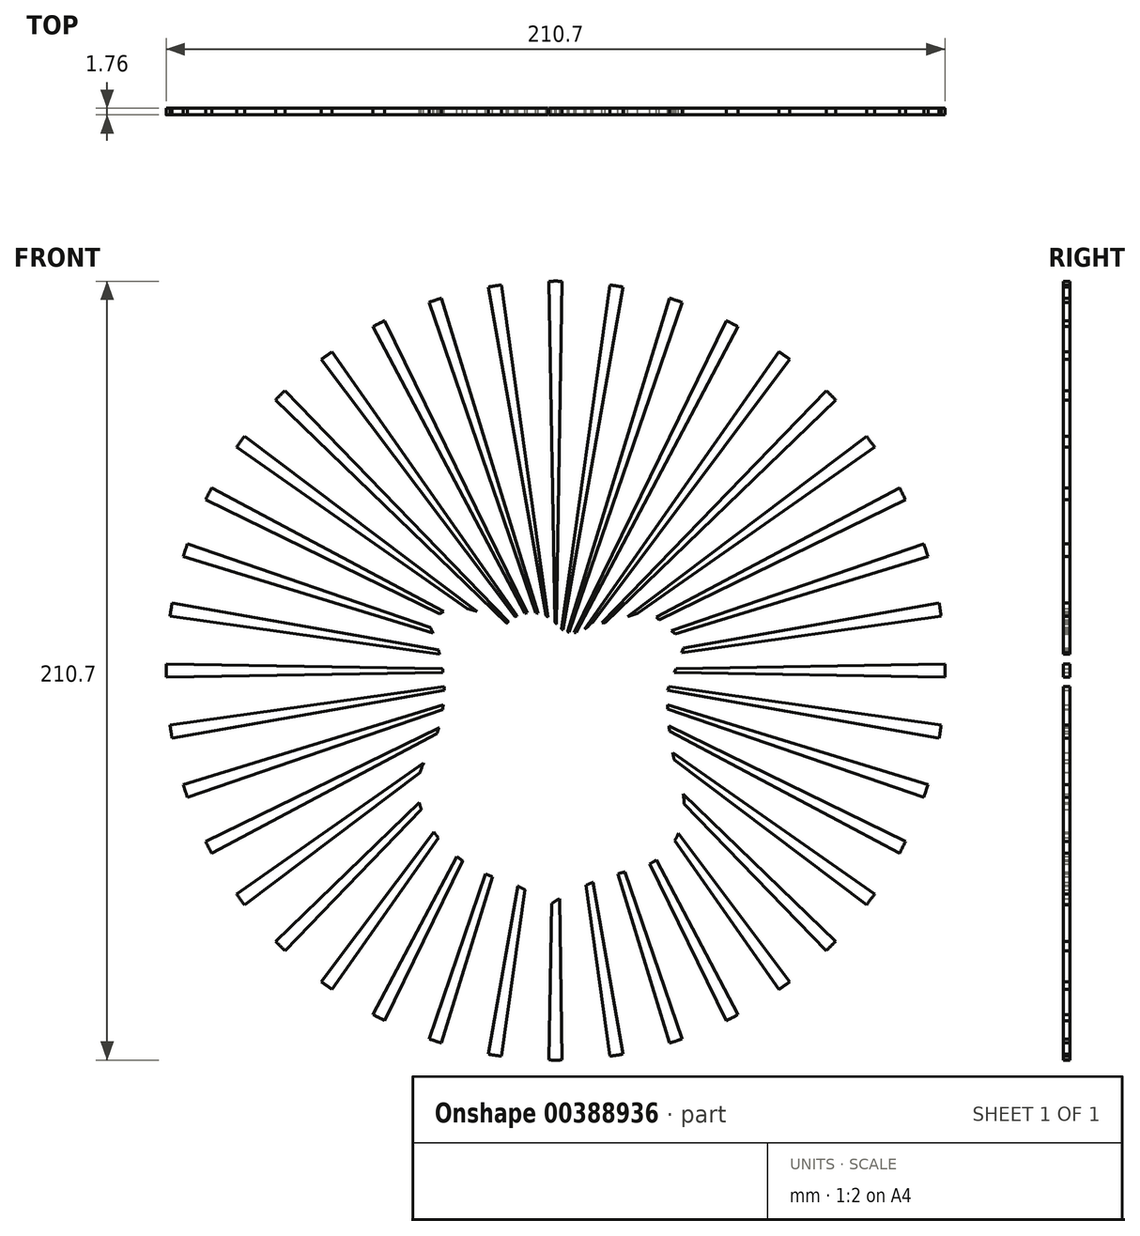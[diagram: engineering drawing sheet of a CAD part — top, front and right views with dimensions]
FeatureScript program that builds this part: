
annotation { "Feature Type Name" : "Feature", "Feature Type Description" : "" }
export const myFeature = defineFeature(function(context is Context, id is Id, definition is map)
    precondition{}
    {
        {
            var Q0;
            Q0=qCreatedBy(makeId("Front.planeOp"),FACE);
            var sketch = newSketch(context, id + "F0", { "sketchPlane" : qUnion([Q0])});
            skCircle(sketch, "E0", {"center": v(1.46, 6.02) * mm, "radius": 39.02 * mm});
            skArc(sketch, "E1", {"start": v(0.74, -17.53) * mm, "mid": v(0.64, -17.44) * mm, "end": v(0.54, -17.36) * mm});
            skArc(sketch, "E2", {"start": v(9.18, -13.96) * mm, "mid": v(8.33, -14.17) * mm, "end": v(7.5, -14.4) * mm});
            skArc(sketch, "E3", {"start": v(9.18, -13.96) * mm, "mid": v(9.38, -13.92) * mm, "end": v(9.59, -13.87) * mm});
            skArc(sketch, "E4", {"start": v(12.7, 4.03) * mm, "mid": v(12.69, 3.1) * mm, "end": v(12.71, 2.18) * mm});
            skArc(sketch, "E5", {"start": v(-10.42, 8.53) * mm, "mid": v(-10.48, 8.8) * mm, "end": v(-10.55, 9.05) * mm});
            skLineSegment(sketch, "E6", {"start": v(-8.79, 12.6) * mm, "end": v(-7.7, 12.3) * mm});
            skLineSegment(sketch, "E7", {"start": v(-4.49, 11.42) * mm, "end": v(-4.05, 10.9) * mm});
            skArc(sketch, "E8", {"start": v(1.46, 10.8) * mm, "mid": v(1.12, 11.12) * mm, "end": v(0.73, 11.38) * mm});
            skArc(sketch, "E9", {"start": v(1.46, 10.8) * mm, "mid": v(1.68, 10.53) * mm, "end": v(1.93, 10.29) * mm});
            skLineSegment(sketch, "E10", {"start": v(5, 10.8) * mm, "end": v(5.12, 10.8) * mm});
            skArc(sketch, "E11", {"start": v(-3.04, -15.26) * mm, "mid": v(-3.45, -15.1) * mm, "end": v(-3.87, -14.95) * mm});
            skArc(sketch, "E12", {"start": v(-1.52, -15.98) * mm, "mid": v(-2.27, -15.6) * mm, "end": v(-3.04, -15.26) * mm});
            skArc(sketch, "E13", {"start": v(-0.45, -16.63) * mm, "mid": v(-0.98, -16.3) * mm, "end": v(-1.52, -15.98) * mm});
            skArc(sketch, "E14", {"start": v(0.54, -17.36) * mm, "mid": v(0.05, -16.98) * mm, "end": v(-0.45, -16.63) * mm});
            skArc(sketch, "E15", {"start": v(3.46, -15.97) * mm, "mid": v(2.08, -16.7) * mm, "end": v(0.74, -17.53) * mm});
            skArc(sketch, "E16", {"start": v(5.93, -14.91) * mm, "mid": v(4.68, -15.4) * mm, "end": v(3.46, -15.97) * mm});
            skArc(sketch, "E17", {"start": v(9.59, -13.87) * mm, "mid": v(13.32, -11.14) * mm, "end": v(14.29, -6.62) * mm});
            skArc(sketch, "E18", {"start": v(13.65, -4.21) * mm, "mid": v(13.84, -4.9) * mm, "end": v(14.04, -5.6) * mm});
            skArc(sketch, "E19", {"start": v(12.96, -0.68) * mm, "mid": v(13.11, -1.71) * mm, "end": v(13.3, -2.74) * mm});
            skArc(sketch, "E20", {"start": v(12.83, 0.44) * mm, "mid": v(12.89, -0.12) * mm, "end": v(12.96, -0.68) * mm});
            skArc(sketch, "E21", {"start": v(12.71, 2.18) * mm, "mid": v(12.76, 1.3) * mm, "end": v(12.83, 0.44) * mm});
            skArc(sketch, "E22", {"start": v(13.3, -2.74) * mm, "mid": v(13.47, -3.48) * mm, "end": v(13.65, -4.21) * mm});
            skArc(sketch, "E23", {"start": v(-12.2, -7.16) * mm, "mid": v(-11.95, -8.05) * mm, "end": v(-11.56, -8.9) * mm});
            skArc(sketch, "E24", {"start": v(-12.34, -6.06) * mm, "mid": v(-12.3, -6.61) * mm, "end": v(-12.2, -7.16) * mm});
            skArc(sketch, "E25", {"start": v(-11.65, -3.01) * mm, "mid": v(-12.18, -4.49) * mm, "end": v(-12.34, -6.06) * mm});
            skArc(sketch, "E26", {"start": v(-11.65, -3.01) * mm, "mid": v(-10.9, -1.56) * mm, "end": v(-10.34, -0.04) * mm});
            skArc(sketch, "E27", {"start": v(-10.34, -0.04) * mm, "mid": v(-10.02, 1.18) * mm, "end": v(-9.82, 2.43) * mm});
            skArc(sketch, "E28", {"start": v(-9.82, 2.43) * mm, "mid": v(-9.73, 3.42) * mm, "end": v(-9.72, 4.4) * mm});
            skArc(sketch, "E29", {"start": v(-11.56, -8.9) * mm, "mid": v(-11.34, -9.27) * mm, "end": v(-11.1, -9.62) * mm});
            skLineSegment(sketch, "E30", {"start": v(5.66, 10.81) * mm, "end": v(6.76, 10.83) * mm});
            skArc(sketch, "E31", {"start": v(3.17, 9.84) * mm, "mid": v(4.22, 10.08) * mm, "end": v(5, 10.8) * mm});
            skArc(sketch, "E32", {"start": v(1.93, 10.29) * mm, "mid": v(2.52, 9.96) * mm, "end": v(3.17, 9.84) * mm});
            skArc(sketch, "E33", {"start": v(0.73, 11.38) * mm, "mid": v(0.12, 11.66) * mm, "end": v(-0.53, 11.8) * mm});
            skArc(sketch, "E34", {"start": v(-0.53, 11.8) * mm, "mid": v(-1.1, 11.83) * mm, "end": v(-1.66, 11.76) * mm});
            skArc(sketch, "E35", {"start": v(-1.66, 11.76) * mm, "mid": v(-2.8, 11.3) * mm, "end": v(-3.69, 10.45) * mm});
            skArc(sketch, "E36", {"start": v(-9.72, 4.4) * mm, "mid": v(-9.76, 5.26) * mm, "end": v(-9.86, 6.11) * mm});
            skArc(sketch, "E37", {"start": v(-10.55, 9.05) * mm, "mid": v(-10.87, 9.9) * mm, "end": v(-11.3, 10.68) * mm});
            skArc(sketch, "E38", {"start": v(-9.86, 6.11) * mm, "mid": v(-9.99, 6.88) * mm, "end": v(-10.16, 7.63) * mm});
            skArc(sketch, "E39", {"start": v(-10.16, 7.63) * mm, "mid": v(-10.28, 8.08) * mm, "end": v(-10.42, 8.53) * mm});
            skArc(sketch, "E40", {"start": v(-11.3, 10.68) * mm, "mid": v(-11.35, 10.78) * mm, "end": v(-11.42, 10.87) * mm});
            skLineSegment(sketch, "E41", {"start": v(-9.47, 12.15) * mm, "end": v(-8.79, 12.6) * mm});
            skLineSegment(sketch, "E42", {"start": v(-11.42, 10.87) * mm, "end": v(-9.47, 12.15) * mm});
            skLineSegment(sketch, "E43", {"start": v(-7.7, 12.3) * mm, "end": v(-6.4, 11.94) * mm});
            skLineSegment(sketch, "E44", {"start": v(-6.4, 11.94) * mm, "end": v(-5.51, 11.7) * mm});
            skLineSegment(sketch, "E45", {"start": v(-5.51, 11.7) * mm, "end": v(-4.49, 11.42) * mm});
            skLineSegment(sketch, "E46", {"start": v(-4.05, 10.9) * mm, "end": v(-3.69, 10.45) * mm});
            skLineSegment(sketch, "E47", {"start": v(-9.48, 12.15) * mm, "end": v(-9.47, 12.15) * mm});
            skLineSegment(sketch, "E48", {"start": v(5.93, -14.91) * mm, "end": v(7.5, -14.4) * mm});
            skArc(sketch, "E49", {"start": v(14.29, -6.62) * mm, "mid": v(14.2, -6.1) * mm, "end": v(14.04, -5.6) * mm});
            skLineSegment(sketch, "E50", {"start": v(6.76, 10.83) * mm, "end": v(10.74, 12.13) * mm});
            skLineSegment(sketch, "E51", {"start": v(10.74, 12.13) * mm, "end": v(14.45, 8.74) * mm});
            skLineSegment(sketch, "E52", {"start": v(14.45, 8.74) * mm, "end": v(12.7, 4.03) * mm});
            skLineSegment(sketch, "E53", {"start": v(5.66, 10.81) * mm, "end": v(5.12, 10.8) * mm});
            skArc(sketch, "E54", {"start": v(-11.1, -9.62) * mm, "mid": v(-7.98, -12.96) * mm, "end": v(-3.87, -14.95) * mm});
            skLineSegment(sketch, "E55", {"start": v(-37.55, 6.68) * mm, "end": v(-9.87, 6.21) * mm});
            skLineSegment(sketch, "E56", {"start": v(-37.55, 5.35) * mm, "end": v(-9.82, 5.83) * mm});
            skLineSegment(sketch, "E57.1.0", {"start": v(-36.97, -0.74) * mm, "end": v(-9.72, 4.05) * mm});
            skLineSegment(sketch, "E57.1.1", {"start": v(-37.17, 0.57) * mm, "end": v(-9.72, 4.44) * mm});
            skLineSegment(sketch, "E57.2.0", {"start": v(-35.44, -6.67) * mm, "end": v(-9.86, 2.13) * mm});
            skLineSegment(sketch, "E57.2.1", {"start": v(-35.85, -5.4) * mm, "end": v(-9.8, 2.57) * mm});
            skLineSegment(sketch, "E57.3.0", {"start": v(-33, -12.29) * mm, "end": v(-10.42, -0.3) * mm});
            skLineSegment(sketch, "E57.3.1", {"start": v(-33.6, -11.1) * mm, "end": v(-10.24, 0.3) * mm});
            skLineSegment(sketch, "E57.4.0", {"start": v(-29.7, -17.45) * mm, "end": v(-12.11, -4.2) * mm});
            skLineSegment(sketch, "E57.4.1", {"start": v(-30.5, -16.37) * mm, "end": v(-11.76, -3.25) * mm});
            skLineSegment(sketch, "E57.5.0", {"start": v(-25.65, -22.04) * mm, "end": v(-12, -7.9) * mm});
            skLineSegment(sketch, "E57.5.1", {"start": v(-26.6, -21.1) * mm, "end": v(-12.2, -7.18) * mm});
            skLineSegment(sketch, "E57.6.0", {"start": v(-20.93, -25.93) * mm, "end": v(-10.29, -10.75) * mm});
            skLineSegment(sketch, "E57.6.1", {"start": v(-22, -25.15) * mm, "end": v(-10.72, -10.17) * mm});
            skLineSegment(sketch, "E57.7.0", {"start": v(-15.66, -29.04) * mm, "end": v(-7.85, -13.05) * mm});
            skLineSegment(sketch, "E57.7.1", {"start": v(-16.84, -28.44) * mm, "end": v(-8.43, -12.6) * mm});
            skLineSegment(sketch, "E57.8.0", {"start": v(-9.96, -31.3) * mm, "end": v(-4.86, -14.63) * mm});
            skLineSegment(sketch, "E57.8.1", {"start": v(-11.23, -30.88) * mm, "end": v(-5.55, -14.36) * mm});
            skLineSegment(sketch, "E57.9.0", {"start": v(-3.98, -32.62) * mm, "end": v(-1.63, -15.92) * mm});
            skLineSegment(sketch, "E57.9.1", {"start": v(-5.3, -32.4) * mm, "end": v(-2.33, -15.57) * mm});
            skLineSegment(sketch, "E57.10.0", {"start": v(2.13, -33) * mm, "end": v(1.85, -16.84) * mm});
            skLineSegment(sketch, "E57.10.1", {"start": v(0.8, -33) * mm, "end": v(1.06, -17.32) * mm});
            skLineSegment(sketch, "E57.11.0", {"start": v(8.22, -32.4) * mm, "end": v(5.2, -15.2) * mm});
            skLineSegment(sketch, "E57.11.1", {"start": v(6.9, -32.62) * mm, "end": v(4.5, -15.5) * mm});
            skLineSegment(sketch, "E57.12.0", {"start": v(14.15, -30.88) * mm, "end": v(8.4, -14.15) * mm});
            skLineSegment(sketch, "E57.12.1", {"start": v(12.89, -31.3) * mm, "end": v(7.7, -14.34) * mm});
            skLineSegment(sketch, "E57.13.0", {"start": v(19.77, -28.44) * mm, "end": v(11.54, -12.96) * mm});
            skLineSegment(sketch, "E57.13.1", {"start": v(18.58, -29.04) * mm, "end": v(10.91, -13.34) * mm});
            skLineSegment(sketch, "E57.14.0", {"start": v(24.93, -25.15) * mm, "end": v(13.76, -10.32) * mm});
            skLineSegment(sketch, "E57.14.1", {"start": v(23.86, -25.93) * mm, "end": v(13.4, -11) * mm});
            skLineSegment(sketch, "E57.15.0", {"start": v(29.52, -21.1) * mm, "end": v(14.25, -6.34) * mm});
            skLineSegment(sketch, "E57.15.1", {"start": v(28.58, -22.04) * mm, "end": v(14.36, -7.32) * mm});
            skLineSegment(sketch, "E57.16.0", {"start": v(33.42, -16.37) * mm, "end": v(13.2, -2.2) * mm});
            skLineSegment(sketch, "E57.16.1", {"start": v(32.63, -17.45) * mm, "end": v(13.34, -2.93) * mm});
            skLineSegment(sketch, "E57.17.0", {"start": v(36.53, -11.1) * mm, "end": v(12.82, 0.47) * mm});
            skLineSegment(sketch, "E57.17.1", {"start": v(35.92, -12.29) * mm, "end": v(12.88, -0.04) * mm});
            skLineSegment(sketch, "E57.18.0", {"start": v(38.77, -5.4) * mm, "end": v(12.7, 2.58) * mm});
            skLineSegment(sketch, "E57.18.1", {"start": v(38.36, -6.67) * mm, "end": v(12.71, 2.15) * mm});
            skLineSegment(sketch, "E57.19.0", {"start": v(40.1, 0.57) * mm, "end": v(12.84, 4.42) * mm});
            skLineSegment(sketch, "E57.19.1", {"start": v(39.9, -0.74) * mm, "end": v(12.7, 4.04) * mm});
            skLineSegment(sketch, "E57.20.0", {"start": v(40.48, 6.68) * mm, "end": v(13.51, 6.23) * mm});
            skLineSegment(sketch, "E57.20.1", {"start": v(40.48, 5.35) * mm, "end": v(13.36, 5.82) * mm});
            skLineSegment(sketch, "E57.21.0", {"start": v(39.9, 12.78) * mm, "end": v(14.28, 8.27) * mm});
            skLineSegment(sketch, "E57.21.1", {"start": v(40.1, 11.47) * mm, "end": v(14.1, 7.8) * mm});
            skLineSegment(sketch, "E57.22.0", {"start": v(38.36, 18.7) * mm, "end": v(13.06, 10) * mm});
            skLineSegment(sketch, "E57.22.1", {"start": v(38.77, 17.44) * mm, "end": v(13.42, 9.68) * mm});
            skLineSegment(sketch, "E57.23.0", {"start": v(35.92, 24.32) * mm, "end": v(11.55, 11.38) * mm});
            skLineSegment(sketch, "E57.23.1", {"start": v(36.53, 23.14) * mm, "end": v(11.86, 11.1) * mm});
            skLineSegment(sketch, "E57.24.0", {"start": v(32.63, 29.49) * mm, "end": v(8.68, 11.45) * mm});
            skLineSegment(sketch, "E57.24.1", {"start": v(33.42, 28.41) * mm, "end": v(9.69, 11.78) * mm});
            skLineSegment(sketch, "E57.25.0", {"start": v(28.58, 34.08) * mm, "end": v(6.1, 10.82) * mm});
            skLineSegment(sketch, "E57.25.1", {"start": v(29.52, 33.14) * mm, "end": v(6.43, 10.82) * mm});
            skLineSegment(sketch, "E57.26.0", {"start": v(23.86, 37.97) * mm, "end": v(4.37, 10.17) * mm});
            skLineSegment(sketch, "E57.27.0", {"start": v(18.58, 41.08) * mm, "end": v(3.33, 9.84) * mm});
            skLineSegment(sketch, "E57.27.1", {"start": v(19.77, 40.48) * mm, "end": v(3.5, 9.85) * mm});
            skLineSegment(sketch, "E57.28.0", {"start": v(12.89, 43.33) * mm, "end": v(2.66, 9.92) * mm});
            skLineSegment(sketch, "E57.28.1", {"start": v(14.15, 42.92) * mm, "end": v(2.8, 9.88) * mm});
            skLineSegment(sketch, "E57.29.0", {"start": v(6.9, 44.66) * mm, "end": v(2.05, 10.2) * mm});
            skLineSegment(sketch, "E57.29.1", {"start": v(8.22, 44.45) * mm, "end": v(2.18, 10.12) * mm});
            skLineSegment(sketch, "E57.30.0", {"start": v(0.8, 45.03) * mm, "end": v(1.38, 10.89) * mm});
            skLineSegment(sketch, "E57.30.1", {"start": v(2.13, 45.03) * mm, "end": v(1.54, 10.7) * mm});
            skLineSegment(sketch, "E57.31.0", {"start": v(-5.3, 44.45) * mm, "end": v(0.5, 11.5) * mm});
            skLineSegment(sketch, "E57.31.1", {"start": v(-3.98, 44.66) * mm, "end": v(0.7, 11.4) * mm});
            skLineSegment(sketch, "E57.32.0", {"start": v(-11.23, 42.92) * mm, "end": v(-0.53, 11.8) * mm});
            skLineSegment(sketch, "E57.32.1", {"start": v(-9.96, 43.33) * mm, "end": v(-0.3, 11.77) * mm});
            skLineSegment(sketch, "E57.33.0", {"start": v(-16.84, 40.48) * mm, "end": v(-1.6, 11.78) * mm});
            skLineSegment(sketch, "E57.33.1", {"start": v(-15.66, 41.08) * mm, "end": v(-1.37, 11.81) * mm});
            skLineSegment(sketch, "E57.34.0", {"start": v(-22, 37.2) * mm, "end": v(-2.6, 11.41) * mm});
            skLineSegment(sketch, "E57.34.1", {"start": v(-20.93, 37.97) * mm, "end": v(-2.4, 11.52) * mm});
            skLineSegment(sketch, "E57.35.0", {"start": v(-26.6, 33.14) * mm, "end": v(-3.44, 10.76) * mm});
            skLineSegment(sketch, "E57.35.1", {"start": v(-25.65, 34.08) * mm, "end": v(-3.27, 10.92) * mm});
            skLineSegment(sketch, "E57.36.0", {"start": v(-30.5, 28.41) * mm, "end": v(-7.38, 12.21) * mm});
            skLineSegment(sketch, "E57.36.1", {"start": v(-29.7, 29.49) * mm, "end": v(-6.4, 11.95) * mm});
            skLineSegment(sketch, "E57.37.0", {"start": v(-33.6, 23.14) * mm, "end": v(-10.16, 11.7) * mm});
            skLineSegment(sketch, "E57.37.1", {"start": v(-33, 24.32) * mm, "end": v(-9.74, 11.97) * mm});
            skLineSegment(sketch, "E57.38.0", {"start": v(-35.85, 17.44) * mm, "end": v(-10.82, 9.78) * mm});
            skLineSegment(sketch, "E57.38.1", {"start": v(-35.44, 18.7) * mm, "end": v(-11.09, 10.34) * mm});
            skLineSegment(sketch, "E57.39.0", {"start": v(-37.17, 11.47) * mm, "end": v(-10.17, 7.66) * mm});
            skLineSegment(sketch, "E57.39.1", {"start": v(-36.97, 12.78) * mm, "end": v(-10.28, 8.09) * mm});
            skLineSegment(sketch, "E58", {"start": v(24.93, 37.2) * mm, "end": v(5.16, 10.8) * mm});
            skPoint(sketch, "E59.orphan", {"position": v(0, 3.93) * mm});
            skSolve(sketch);
        }
        {
            var Q0;
            {var subQ0=sQuery(id+"F0.wireOp",EDGE,"E57.21.0");Q0=makeQuery(id+"F0.imprint","IMPRINT",FACE,{"disambiguationData":[TD([[makeQuery(id+"F0.imprint","IMPRINT",EDGE,{"derivedFrom":subQ0}),1.0]])]});}
            var Q1;
            {var subQ0=sQuery(id+"F0.wireOp",EDGE,"E57.22.0");Q1=makeQuery(id+"F0.imprint","IMPRINT",FACE,{"disambiguationData":[TD([[makeQuery(id+"F0.imprint","IMPRINT",EDGE,{"derivedFrom":subQ0}),1.0]])]});}
            var Q2;
            {var subQ0=sQuery(id+"F0.wireOp",EDGE,"E57.23.0");Q2=makeQuery(id+"F0.imprint","IMPRINT",FACE,{"disambiguationData":[TD([[makeQuery(id+"F0.imprint","IMPRINT",EDGE,{"derivedFrom":subQ0}),1.0]])]});}
            var Q3;
            {var subQ0=sQuery(id+"F0.wireOp",EDGE,"E57.24.0");Q3=makeQuery(id+"F0.imprint","IMPRINT",FACE,{"disambiguationData":[TD([[makeQuery(id+"F0.imprint","IMPRINT",EDGE,{"derivedFrom":subQ0}),1.0]])]});}
            var Q4;
            {var subQ0=sQuery(id+"F0.wireOp",EDGE,"E57.25.0");Q4=makeQuery(id+"F0.imprint","IMPRINT",FACE,{"disambiguationData":[TD([[makeQuery(id+"F0.imprint","IMPRINT",EDGE,{"derivedFrom":subQ0}),1.0]])]});}
            var Q5;
            {var subQ1=sQuery(id+"F0.wireOp",EDGE,"E10");Q5=makeQuery(id+"F0.imprint","IMPRINT",FACE,{"disambiguationData":[TD([[makeQuery(id+"F0.imprint","IMPRINT",EDGE,{"derivedFrom":subQ1}),1.0]])]});}
            var Q6;
            {var subQ0=sQuery(id+"F0.wireOp",EDGE,"E57.27.0");Q6=makeQuery(id+"F0.imprint","IMPRINT",FACE,{"disambiguationData":[TD([[makeQuery(id+"F0.imprint","IMPRINT",EDGE,{"derivedFrom":subQ0}),1.0]])]});}
            var Q7;
            {var subQ0=sQuery(id+"F0.wireOp",EDGE,"E57.28.0");Q7=makeQuery(id+"F0.imprint","IMPRINT",FACE,{"disambiguationData":[TD([[makeQuery(id+"F0.imprint","IMPRINT",EDGE,{"derivedFrom":subQ0}),1.0]])]});}
            var Q8;
            {var subQ0=sQuery(id+"F0.wireOp",EDGE,"E57.29.0");Q8=makeQuery(id+"F0.imprint","IMPRINT",FACE,{"disambiguationData":[TD([[makeQuery(id+"F0.imprint","IMPRINT",EDGE,{"derivedFrom":subQ0}),1.0]])]});}
            var Q9;
            {var subQ0=sQuery(id+"F0.wireOp",EDGE,"E57.30.0");Q9=makeQuery(id+"F0.imprint","IMPRINT",FACE,{"disambiguationData":[TD([[makeQuery(id+"F0.imprint","IMPRINT",EDGE,{"derivedFrom":subQ0}),1.0]])]});}
            var Q10;
            {var subQ0=sQuery(id+"F0.wireOp",EDGE,"E57.31.0");Q10=makeQuery(id+"F0.imprint","IMPRINT",FACE,{"disambiguationData":[TD([[makeQuery(id+"F0.imprint","IMPRINT",EDGE,{"derivedFrom":subQ0}),1.0]])]});}
            var Q11;
            {var subQ0=sQuery(id+"F0.wireOp",EDGE,"E57.32.0");Q11=makeQuery(id+"F0.imprint","IMPRINT",FACE,{"disambiguationData":[TD([[makeQuery(id+"F0.imprint","IMPRINT",EDGE,{"derivedFrom":subQ0}),1.0]])]});}
            var Q12;
            {var subQ0=sQuery(id+"F0.wireOp",EDGE,"E57.33.0");Q12=makeQuery(id+"F0.imprint","IMPRINT",FACE,{"disambiguationData":[TD([[makeQuery(id+"F0.imprint","IMPRINT",EDGE,{"derivedFrom":subQ0}),1.0]])]});}
            var Q13;
            {var subQ0=sQuery(id+"F0.wireOp",EDGE,"E57.34.0");Q13=makeQuery(id+"F0.imprint","IMPRINT",FACE,{"disambiguationData":[TD([[makeQuery(id+"F0.imprint","IMPRINT",EDGE,{"derivedFrom":subQ0}),1.0]])]});}
            var Q14;
            {var subQ0=sQuery(id+"F0.wireOp",EDGE,"E57.35.0");Q14=makeQuery(id+"F0.imprint","IMPRINT",FACE,{"disambiguationData":[TD([[makeQuery(id+"F0.imprint","IMPRINT",EDGE,{"derivedFrom":subQ0}),1.0]])]});}
            var Q15;
            {var subQ0=sQuery(id+"F0.wireOp",EDGE,"E57.36.0");Q15=makeQuery(id+"F0.imprint","IMPRINT",FACE,{"disambiguationData":[TD([[makeQuery(id+"F0.imprint","IMPRINT",EDGE,{"derivedFrom":subQ0}),1.0]])]});}
            var Q16;
            {var subQ0=sQuery(id+"F0.wireOp",EDGE,"E57.37.0");Q16=makeQuery(id+"F0.imprint","IMPRINT",FACE,{"disambiguationData":[TD([[makeQuery(id+"F0.imprint","IMPRINT",EDGE,{"derivedFrom":subQ0}),1.0]])]});}
            var Q17;
            {var subQ0=sQuery(id+"F0.wireOp",EDGE,"E57.38.0");Q17=makeQuery(id+"F0.imprint","IMPRINT",FACE,{"disambiguationData":[TD([[makeQuery(id+"F0.imprint","IMPRINT",EDGE,{"derivedFrom":subQ0}),1.0]])]});}
            var Q18;
            {var subQ0=sQuery(id+"F0.wireOp",EDGE,"E55");Q18=makeQuery(id+"F0.imprint","IMPRINT",FACE,{"disambiguationData":[TD([[makeQuery(id+"F0.imprint","IMPRINT",EDGE,{"derivedFrom":subQ0}),-1.0]])]});}
            var Q19;
            {var subQ0=sQuery(id+"F0.wireOp",EDGE,"E57.1.0");Q19=makeQuery(id+"F0.imprint","IMPRINT",FACE,{"disambiguationData":[TD([[makeQuery(id+"F0.imprint","IMPRINT",EDGE,{"derivedFrom":subQ0}),1.0]])]});}
            var Q20;
            {var subQ0=sQuery(id+"F0.wireOp",EDGE,"E57.2.0");Q20=makeQuery(id+"F0.imprint","IMPRINT",FACE,{"disambiguationData":[TD([[makeQuery(id+"F0.imprint","IMPRINT",EDGE,{"derivedFrom":subQ0}),1.0]])]});}
            var Q21;
            {var subQ0=sQuery(id+"F0.wireOp",EDGE,"E57.3.0");Q21=makeQuery(id+"F0.imprint","IMPRINT",FACE,{"disambiguationData":[TD([[makeQuery(id+"F0.imprint","IMPRINT",EDGE,{"derivedFrom":subQ0}),1.0]])]});}
            var Q22;
            {var subQ0=sQuery(id+"F0.wireOp",EDGE,"E57.4.0");Q22=makeQuery(id+"F0.imprint","IMPRINT",FACE,{"disambiguationData":[TD([[makeQuery(id+"F0.imprint","IMPRINT",EDGE,{"derivedFrom":subQ0}),1.0]])]});}
            var Q23;
            {var subQ0=sQuery(id+"F0.wireOp",EDGE,"E57.5.0");Q23=makeQuery(id+"F0.imprint","IMPRINT",FACE,{"disambiguationData":[TD([[makeQuery(id+"F0.imprint","IMPRINT",EDGE,{"derivedFrom":subQ0}),1.0]])]});}
            var Q24;
            {var subQ0=sQuery(id+"F0.wireOp",EDGE,"E57.6.0");Q24=makeQuery(id+"F0.imprint","IMPRINT",FACE,{"disambiguationData":[TD([[makeQuery(id+"F0.imprint","IMPRINT",EDGE,{"derivedFrom":subQ0}),1.0]])]});}
            var Q25;
            {var subQ0=sQuery(id+"F0.wireOp",EDGE,"E57.7.0");Q25=makeQuery(id+"F0.imprint","IMPRINT",FACE,{"disambiguationData":[TD([[makeQuery(id+"F0.imprint","IMPRINT",EDGE,{"derivedFrom":subQ0}),1.0]])]});}
            var Q26;
            {var subQ0=sQuery(id+"F0.wireOp",EDGE,"E57.8.0");Q26=makeQuery(id+"F0.imprint","IMPRINT",FACE,{"disambiguationData":[TD([[makeQuery(id+"F0.imprint","IMPRINT",EDGE,{"derivedFrom":subQ0}),1.0]])]});}
            var Q27;
            {var subQ0=sQuery(id+"F0.wireOp",EDGE,"E57.9.0");Q27=makeQuery(id+"F0.imprint","IMPRINT",FACE,{"disambiguationData":[TD([[makeQuery(id+"F0.imprint","IMPRINT",EDGE,{"derivedFrom":subQ0}),1.0]])]});}
            var Q28;
            {var subQ0=sQuery(id+"F0.wireOp",EDGE,"E57.10.0");Q28=makeQuery(id+"F0.imprint","IMPRINT",FACE,{"disambiguationData":[TD([[makeQuery(id+"F0.imprint","IMPRINT",EDGE,{"derivedFrom":subQ0}),1.0]])]});}
            var Q29;
            {var subQ0=sQuery(id+"F0.wireOp",EDGE,"E57.11.0");Q29=makeQuery(id+"F0.imprint","IMPRINT",FACE,{"disambiguationData":[TD([[makeQuery(id+"F0.imprint","IMPRINT",EDGE,{"derivedFrom":subQ0}),1.0]])]});}
            var Q30;
            {var subQ0=sQuery(id+"F0.wireOp",EDGE,"E57.12.0");Q30=makeQuery(id+"F0.imprint","IMPRINT",FACE,{"disambiguationData":[TD([[makeQuery(id+"F0.imprint","IMPRINT",EDGE,{"derivedFrom":subQ0}),1.0]])]});}
            var Q31;
            {var subQ0=sQuery(id+"F0.wireOp",EDGE,"E57.13.0");Q31=makeQuery(id+"F0.imprint","IMPRINT",FACE,{"disambiguationData":[TD([[makeQuery(id+"F0.imprint","IMPRINT",EDGE,{"derivedFrom":subQ0}),1.0]])]});}
            var Q32;
            {var subQ0=sQuery(id+"F0.wireOp",EDGE,"E57.14.0");Q32=makeQuery(id+"F0.imprint","IMPRINT",FACE,{"disambiguationData":[TD([[makeQuery(id+"F0.imprint","IMPRINT",EDGE,{"derivedFrom":subQ0}),1.0]])]});}
            var Q33;
            {var subQ0=sQuery(id+"F0.wireOp",EDGE,"E57.15.0");Q33=makeQuery(id+"F0.imprint","IMPRINT",FACE,{"disambiguationData":[TD([[makeQuery(id+"F0.imprint","IMPRINT",EDGE,{"derivedFrom":subQ0}),1.0]])]});}
            var Q34;
            {var subQ0=sQuery(id+"F0.wireOp",EDGE,"E57.16.0");Q34=makeQuery(id+"F0.imprint","IMPRINT",FACE,{"disambiguationData":[TD([[makeQuery(id+"F0.imprint","IMPRINT",EDGE,{"derivedFrom":subQ0}),1.0]])]});}
            var Q35;
            {var subQ3=sQuery(id+"F0.wireOp",EDGE,"E57.17.0");Q35=makeQuery(id+"F0.imprint","IMPRINT",FACE,{"disambiguationData":[TD([[makeQuery(id+"F0.imprint","IMPRINT",EDGE,{"derivedFrom":subQ3}),1.0]])]});}
            var Q36;
            {var subQ0=sQuery(id+"F0.wireOp",EDGE,"E57.18.0");Q36=makeQuery(id+"F0.imprint","IMPRINT",FACE,{"disambiguationData":[TD([[makeQuery(id+"F0.imprint","IMPRINT",EDGE,{"derivedFrom":subQ0}),1.0]])]});}
            var Q37;
            {var subQ0=sQuery(id+"F0.wireOp",EDGE,"E57.19.0");Q37=makeQuery(id+"F0.imprint","IMPRINT",FACE,{"disambiguationData":[TD([[makeQuery(id+"F0.imprint","IMPRINT",EDGE,{"derivedFrom":subQ0}),1.0]])]});}
            var Q38;
            {var subQ0=sQuery(id+"F0.wireOp",EDGE,"E57.20.0");Q38=makeQuery(id+"F0.imprint","IMPRINT",FACE,{"disambiguationData":[TD([[makeQuery(id+"F0.imprint","IMPRINT",EDGE,{"derivedFrom":subQ0}),1.0]])]});}
            var Q39;
            {var subQ0=sQuery(id+"F0.wireOp",EDGE,"E57.39.0");Q39=makeQuery(id+"F0.imprint","IMPRINT",FACE,{"disambiguationData":[TD([[makeQuery(id+"F0.imprint","IMPRINT",EDGE,{"derivedFrom":subQ0}),1.0]])]});}
            extrude(context, id + "F1", {"entities" : qUnion([Q0, Q1, Q2, Q3, Q4, Q5, Q6, Q7, Q8, Q9, Q10, Q11, Q12, Q13, Q14, Q15, Q16, Q17, Q18, Q19, Q20, Q21, Q22, Q23, Q24, Q25, Q26, Q27, Q28, Q29, Q30, Q31, Q32, Q33, Q34, Q35, Q36, Q37, Q38, Q39]), "depth" : 0.65 * mm});
        }
        {
            var Q0;
            Q0=makeQuery(id+"F1.opExtrude","SWEPT_BODY",BODY,{"disambiguationData":[OSD([sQuery(id+"F0.wireOp",EDGE,"E0"),sQuery(id+"F0.wireOp",EDGE,"E51"),sQuery(id+"F0.wireOp",EDGE,"E57.22.0"),sQuery(id+"F0.wireOp",EDGE,"E57.22.1")])]});
            var Q1;
            Q1=makeQuery(id+"F1.opExtrude","SWEPT_BODY",BODY,{"disambiguationData":[OSD([sQuery(id+"F0.wireOp",EDGE,"E0"),sQuery(id+"F0.wireOp",EDGE,"E35"),sQuery(id+"F0.wireOp",EDGE,"E57.35.0"),sQuery(id+"F0.wireOp",EDGE,"E57.35.1")])]});
            var Q2;
            Q2=makeQuery(id+"F1.opExtrude","SWEPT_BODY",BODY,{"disambiguationData":[OSD([sQuery(id+"F0.wireOp",EDGE,"E0"),sQuery(id+"F0.wireOp",EDGE,"E42"),sQuery(id+"F0.wireOp",EDGE,"E57.37.0"),sQuery(id+"F0.wireOp",EDGE,"E57.37.1")])]});
            var Q3;
            Q3=makeQuery(id+"F1.opExtrude","SWEPT_BODY",BODY,{"disambiguationData":[OSD([sQuery(id+"F0.wireOp",EDGE,"E0"),sQuery(id+"F0.wireOp",EDGE,"E32"),sQuery(id+"F0.wireOp",EDGE,"E57.29.0"),sQuery(id+"F0.wireOp",EDGE,"E57.29.1")])]});
            var Q4;
            Q4=makeQuery(id+"F1.opExtrude","SWEPT_BODY",BODY,{"disambiguationData":[OSD([sQuery(id+"F0.wireOp",EDGE,"E0"),sQuery(id+"F0.wireOp",EDGE,"E52"),sQuery(id+"F0.wireOp",EDGE,"E57.21.0"),sQuery(id+"F0.wireOp",EDGE,"E57.21.1")])]});
            var Q5;
            Q5=makeQuery(id+"F1.opExtrude","SWEPT_BODY",BODY,{"disambiguationData":[OSD([sQuery(id+"F0.wireOp",EDGE,"E0"),sQuery(id+"F0.wireOp",EDGE,"E32"),sQuery(id+"F0.wireOp",EDGE,"E57.28.0"),sQuery(id+"F0.wireOp",EDGE,"E57.28.1")])]});
            var Q6;
            Q6=makeQuery(id+"F1.opExtrude","SWEPT_BODY",BODY,{"disambiguationData":[OSD([sQuery(id+"F0.wireOp",EDGE,"E0"),sQuery(id+"F0.wireOp",EDGE,"E37"),sQuery(id+"F0.wireOp",EDGE,"E57.38.0"),sQuery(id+"F0.wireOp",EDGE,"E57.38.1")])]});
            var Q7;
            Q7=makeQuery(id+"F1.opExtrude","SWEPT_BODY",BODY,{"disambiguationData":[OSD([sQuery(id+"F0.wireOp",EDGE,"E0"),sQuery(id+"F0.wireOp",EDGE,"E43"),sQuery(id+"F0.wireOp",EDGE,"E57.36.0"),sQuery(id+"F0.wireOp",EDGE,"E57.36.1")])]});
            var Q8;
            Q8=makeQuery(id+"F1.opExtrude","SWEPT_BODY",BODY,{"disambiguationData":[OSD([sQuery(id+"F0.wireOp",EDGE,"E0"),sQuery(id+"F0.wireOp",EDGE,"E39"),sQuery(id+"F0.wireOp",EDGE,"E57.39.0"),sQuery(id+"F0.wireOp",EDGE,"E57.39.1")])]});
            var Q9;
            Q9=makeQuery(id+"F1.opExtrude","SWEPT_BODY",BODY,{"disambiguationData":[OSD([sQuery(id+"F0.wireOp",EDGE,"E0"),sQuery(id+"F0.wireOp",EDGE,"E36"),sQuery(id+"F0.wireOp",EDGE,"E38"),sQuery(id+"F0.wireOp",EDGE,"E55"),sQuery(id+"F0.wireOp",EDGE,"E56")])]});
            var Q10;
            Q10=makeQuery(id+"F1.opExtrude","SWEPT_BODY",BODY,{"disambiguationData":[OSD([sQuery(id+"F0.wireOp",EDGE,"E0"),sQuery(id+"F0.wireOp",EDGE,"E28"),sQuery(id+"F0.wireOp",EDGE,"E36"),sQuery(id+"F0.wireOp",EDGE,"E57.1.0"),sQuery(id+"F0.wireOp",EDGE,"E57.1.1")])]});
            var Q11;
            Q11=makeQuery(id+"F1.opExtrude","SWEPT_BODY",BODY,{"disambiguationData":[OSD([sQuery(id+"F0.wireOp",EDGE,"E0"),sQuery(id+"F0.wireOp",EDGE,"E27"),sQuery(id+"F0.wireOp",EDGE,"E28"),sQuery(id+"F0.wireOp",EDGE,"E57.2.0"),sQuery(id+"F0.wireOp",EDGE,"E57.2.1")])]});
            var Q12;
            Q12=makeQuery(id+"F1.opExtrude","SWEPT_BODY",BODY,{"disambiguationData":[OSD([sQuery(id+"F0.wireOp",EDGE,"E0"),sQuery(id+"F0.wireOp",EDGE,"E26"),sQuery(id+"F0.wireOp",EDGE,"E27"),sQuery(id+"F0.wireOp",EDGE,"E57.3.0"),sQuery(id+"F0.wireOp",EDGE,"E57.3.1")])]});
            var Q13;
            Q13=makeQuery(id+"F1.opExtrude","SWEPT_BODY",BODY,{"disambiguationData":[OSD([sQuery(id+"F0.wireOp",EDGE,"E0"),sQuery(id+"F0.wireOp",EDGE,"E25"),sQuery(id+"F0.wireOp",EDGE,"E57.4.0"),sQuery(id+"F0.wireOp",EDGE,"E57.4.1")])]});
            var Q14;
            Q14=makeQuery(id+"F1.opExtrude","SWEPT_BODY",BODY,{"disambiguationData":[OSD([sQuery(id+"F0.wireOp",EDGE,"E0"),sQuery(id+"F0.wireOp",EDGE,"E23"),sQuery(id+"F0.wireOp",EDGE,"E57.5.0"),sQuery(id+"F0.wireOp",EDGE,"E57.5.1")])]});
            var Q15;
            Q15=makeQuery(id+"F1.opExtrude","SWEPT_BODY",BODY,{"disambiguationData":[OSD([sQuery(id+"F0.wireOp",EDGE,"E0"),sQuery(id+"F0.wireOp",EDGE,"E54"),sQuery(id+"F0.wireOp",EDGE,"E57.6.0"),sQuery(id+"F0.wireOp",EDGE,"E57.6.1")])]});
            var Q16;
            Q16=makeQuery(id+"F1.opExtrude","SWEPT_BODY",BODY,{"disambiguationData":[OSD([sQuery(id+"F0.wireOp",EDGE,"E0"),sQuery(id+"F0.wireOp",EDGE,"E54"),sQuery(id+"F0.wireOp",EDGE,"E57.7.0"),sQuery(id+"F0.wireOp",EDGE,"E57.7.1")])]});
            var Q17;
            Q17=makeQuery(id+"F1.opExtrude","SWEPT_BODY",BODY,{"disambiguationData":[OSD([sQuery(id+"F0.wireOp",EDGE,"E0"),sQuery(id+"F0.wireOp",EDGE,"E54"),sQuery(id+"F0.wireOp",EDGE,"E57.8.0"),sQuery(id+"F0.wireOp",EDGE,"E57.8.1")])]});
            var Q18;
            Q18=makeQuery(id+"F1.opExtrude","SWEPT_BODY",BODY,{"disambiguationData":[OSD([sQuery(id+"F0.wireOp",EDGE,"E0"),sQuery(id+"F0.wireOp",EDGE,"E12"),sQuery(id+"F0.wireOp",EDGE,"E57.9.0"),sQuery(id+"F0.wireOp",EDGE,"E57.9.1")])]});
            var Q19;
            Q19=makeQuery(id+"F1.opExtrude","SWEPT_BODY",BODY,{"disambiguationData":[OSD([sQuery(id+"F0.wireOp",EDGE,"E0"),sQuery(id+"F0.wireOp",EDGE,"E15"),sQuery(id+"F0.wireOp",EDGE,"E57.10.0"),sQuery(id+"F0.wireOp",EDGE,"E57.10.1")])]});
            var Q20;
            Q20=makeQuery(id+"F1.opExtrude","SWEPT_BODY",BODY,{"disambiguationData":[OSD([sQuery(id+"F0.wireOp",EDGE,"E0"),sQuery(id+"F0.wireOp",EDGE,"E16"),sQuery(id+"F0.wireOp",EDGE,"E57.11.0"),sQuery(id+"F0.wireOp",EDGE,"E57.11.1")])]});
            var Q21;
            Q21=makeQuery(id+"F1.opExtrude","SWEPT_BODY",BODY,{"disambiguationData":[OSD([sQuery(id+"F0.wireOp",EDGE,"E0"),sQuery(id+"F0.wireOp",EDGE,"E2"),sQuery(id+"F0.wireOp",EDGE,"E57.12.0"),sQuery(id+"F0.wireOp",EDGE,"E57.12.1")])]});
            var Q22;
            Q22=makeQuery(id+"F1.opExtrude","SWEPT_BODY",BODY,{"disambiguationData":[OSD([sQuery(id+"F0.wireOp",EDGE,"E0"),sQuery(id+"F0.wireOp",EDGE,"E17"),sQuery(id+"F0.wireOp",EDGE,"E57.13.0"),sQuery(id+"F0.wireOp",EDGE,"E57.13.1")])]});
            var Q23;
            Q23=makeQuery(id+"F1.opExtrude","SWEPT_BODY",BODY,{"disambiguationData":[OSD([sQuery(id+"F0.wireOp",EDGE,"E0"),sQuery(id+"F0.wireOp",EDGE,"E17"),sQuery(id+"F0.wireOp",EDGE,"E57.14.0"),sQuery(id+"F0.wireOp",EDGE,"E57.14.1")])]});
            var Q24;
            Q24=makeQuery(id+"F1.opExtrude","SWEPT_BODY",BODY,{"disambiguationData":[OSD([sQuery(id+"F0.wireOp",EDGE,"E0"),sQuery(id+"F0.wireOp",EDGE,"E17"),sQuery(id+"F0.wireOp",EDGE,"E49"),sQuery(id+"F0.wireOp",EDGE,"E57.15.0"),sQuery(id+"F0.wireOp",EDGE,"E57.15.1")])]});
            var Q25;
            Q25=makeQuery(id+"F1.opExtrude","SWEPT_BODY",BODY,{"disambiguationData":[OSD([sQuery(id+"F0.wireOp",EDGE,"E0"),sQuery(id+"F0.wireOp",EDGE,"E19"),sQuery(id+"F0.wireOp",EDGE,"E22"),sQuery(id+"F0.wireOp",EDGE,"E57.16.0"),sQuery(id+"F0.wireOp",EDGE,"E57.16.1")])]});
            var Q26;
            Q26=makeQuery(id+"F1.opExtrude","SWEPT_BODY",BODY,{"disambiguationData":[OSD([sQuery(id+"F0.wireOp",EDGE,"E0"),sQuery(id+"F0.wireOp",EDGE,"E20"),sQuery(id+"F0.wireOp",EDGE,"E21"),sQuery(id+"F0.wireOp",EDGE,"E57.17.0"),sQuery(id+"F0.wireOp",EDGE,"E57.17.1")])]});
            var Q27;
            Q27=makeQuery(id+"F1.opExtrude","SWEPT_BODY",BODY,{"disambiguationData":[OSD([sQuery(id+"F0.wireOp",EDGE,"E0"),sQuery(id+"F0.wireOp",EDGE,"E4"),sQuery(id+"F0.wireOp",EDGE,"E21"),sQuery(id+"F0.wireOp",EDGE,"E57.18.0"),sQuery(id+"F0.wireOp",EDGE,"E57.18.1")])]});
            var Q28;
            Q28=makeQuery(id+"F1.opExtrude","SWEPT_BODY",BODY,{"disambiguationData":[OSD([sQuery(id+"F0.wireOp",EDGE,"E0"),sQuery(id+"F0.wireOp",EDGE,"E52"),sQuery(id+"F0.wireOp",EDGE,"E57.19.0"),sQuery(id+"F0.wireOp",EDGE,"E57.19.1")])]});
            var Q29;
            Q29=makeQuery(id+"F1.opExtrude","SWEPT_BODY",BODY,{"disambiguationData":[OSD([sQuery(id+"F0.wireOp",EDGE,"E0"),sQuery(id+"F0.wireOp",EDGE,"E52"),sQuery(id+"F0.wireOp",EDGE,"E57.20.0"),sQuery(id+"F0.wireOp",EDGE,"E57.20.1")])]});
            var Q30;
            Q30=makeQuery(id+"F1.opExtrude","SWEPT_BODY",BODY,{"disambiguationData":[OSD([sQuery(id+"F0.wireOp",EDGE,"E0"),sQuery(id+"F0.wireOp",EDGE,"E50"),sQuery(id+"F0.wireOp",EDGE,"E57.24.0"),sQuery(id+"F0.wireOp",EDGE,"E57.24.1")])]});
            var Q31;
            Q31=makeQuery(id+"F1.opExtrude","SWEPT_BODY",BODY,{"disambiguationData":[OSD([sQuery(id+"F0.wireOp",EDGE,"E0"),sQuery(id+"F0.wireOp",EDGE,"E30"),sQuery(id+"F0.wireOp",EDGE,"E57.25.0"),sQuery(id+"F0.wireOp",EDGE,"E57.25.1")])]});
            var Q32;
            Q32=makeQuery(id+"F1.opExtrude","SWEPT_BODY",BODY,{"disambiguationData":[OSD([sQuery(id+"F0.wireOp",EDGE,"E0"),sQuery(id+"F0.wireOp",EDGE,"E31"),sQuery(id+"F0.wireOp",EDGE,"E57.27.0"),sQuery(id+"F0.wireOp",EDGE,"E57.27.1")])]});
            var Q33;
            Q33=makeQuery(id+"F1.opExtrude","SWEPT_BODY",BODY,{"disambiguationData":[OSD([sQuery(id+"F0.wireOp",EDGE,"E0"),sQuery(id+"F0.wireOp",EDGE,"E51"),sQuery(id+"F0.wireOp",EDGE,"E57.23.0"),sQuery(id+"F0.wireOp",EDGE,"E57.23.1")])]});
            var Q34;
            Q34=makeQuery(id+"F1.opExtrude","SWEPT_BODY",BODY,{"disambiguationData":[OSD([sQuery(id+"F0.wireOp",EDGE,"E0"),sQuery(id+"F0.wireOp",EDGE,"E34"),sQuery(id+"F0.wireOp",EDGE,"E57.33.0"),sQuery(id+"F0.wireOp",EDGE,"E57.33.1")])]});
            var Q35;
            Q35=makeQuery(id+"F1.opExtrude","SWEPT_BODY",BODY,{"disambiguationData":[OSD([sQuery(id+"F0.wireOp",EDGE,"E0"),sQuery(id+"F0.wireOp",EDGE,"E8"),sQuery(id+"F0.wireOp",EDGE,"E9"),sQuery(id+"F0.wireOp",EDGE,"E57.30.0"),sQuery(id+"F0.wireOp",EDGE,"E57.30.1")])]});
            var Q36;
            Q36=makeQuery(id+"F1.opExtrude","SWEPT_BODY",BODY,{"disambiguationData":[OSD([sQuery(id+"F0.wireOp",EDGE,"E0"),sQuery(id+"F0.wireOp",EDGE,"E33"),sQuery(id+"F0.wireOp",EDGE,"E57.31.0"),sQuery(id+"F0.wireOp",EDGE,"E57.31.1")])]});
            var Q37;
            Q37=makeQuery(id+"F1.opExtrude","SWEPT_BODY",BODY,{"disambiguationData":[OSD([sQuery(id+"F0.wireOp",EDGE,"E0"),sQuery(id+"F0.wireOp",EDGE,"E35"),sQuery(id+"F0.wireOp",EDGE,"E57.34.0"),sQuery(id+"F0.wireOp",EDGE,"E57.34.1")])]});
            var Q38;
            Q38=makeQuery(id+"F1.opExtrude","SWEPT_BODY",BODY,{"disambiguationData":[OSD([sQuery(id+"F0.wireOp",EDGE,"E0"),sQuery(id+"F0.wireOp",EDGE,"E33"),sQuery(id+"F0.wireOp",EDGE,"E57.32.0"),sQuery(id+"F0.wireOp",EDGE,"E57.32.1")])]});
            var Q39;
            Q39=makeQuery(id+"F1.opExtrude","SWEPT_BODY",BODY,{"disambiguationData":[OSD([sQuery(id+"F0.wireOp",EDGE,"E0"),sQuery(id+"F0.wireOp",EDGE,"E10"),sQuery(id+"F0.wireOp",EDGE,"E31"),sQuery(id+"F0.wireOp",EDGE,"E53"),sQuery(id+"F0.wireOp",EDGE,"E57.26.0"),sQuery(id+"F0.wireOp",EDGE,"E58")])]});
            var Q40;
            Q40=qCreatedBy(makeId("Origin.pointOp"),VERTEX);
            transform(context, id + "F2", {"entities" : qUnion([Q0, Q1, Q2, Q3, Q4, Q5, Q6, Q7, Q8, Q9, Q10, Q11, Q12, Q13, Q14, Q15, Q16, Q17, Q18, Q19, Q20, Q21, Q22, Q23, Q24, Q25, Q26, Q27, Q28, Q29, Q30, Q31, Q32, Q33, Q34, Q35, Q36, Q37, Q38, Q39]), "transformType" : TransformType.SCALE_UNIFORMLY, "scale" : 2.7, "scalePoint" : qUnion([Q40]), "makeCopy" : false});
        }
    });
